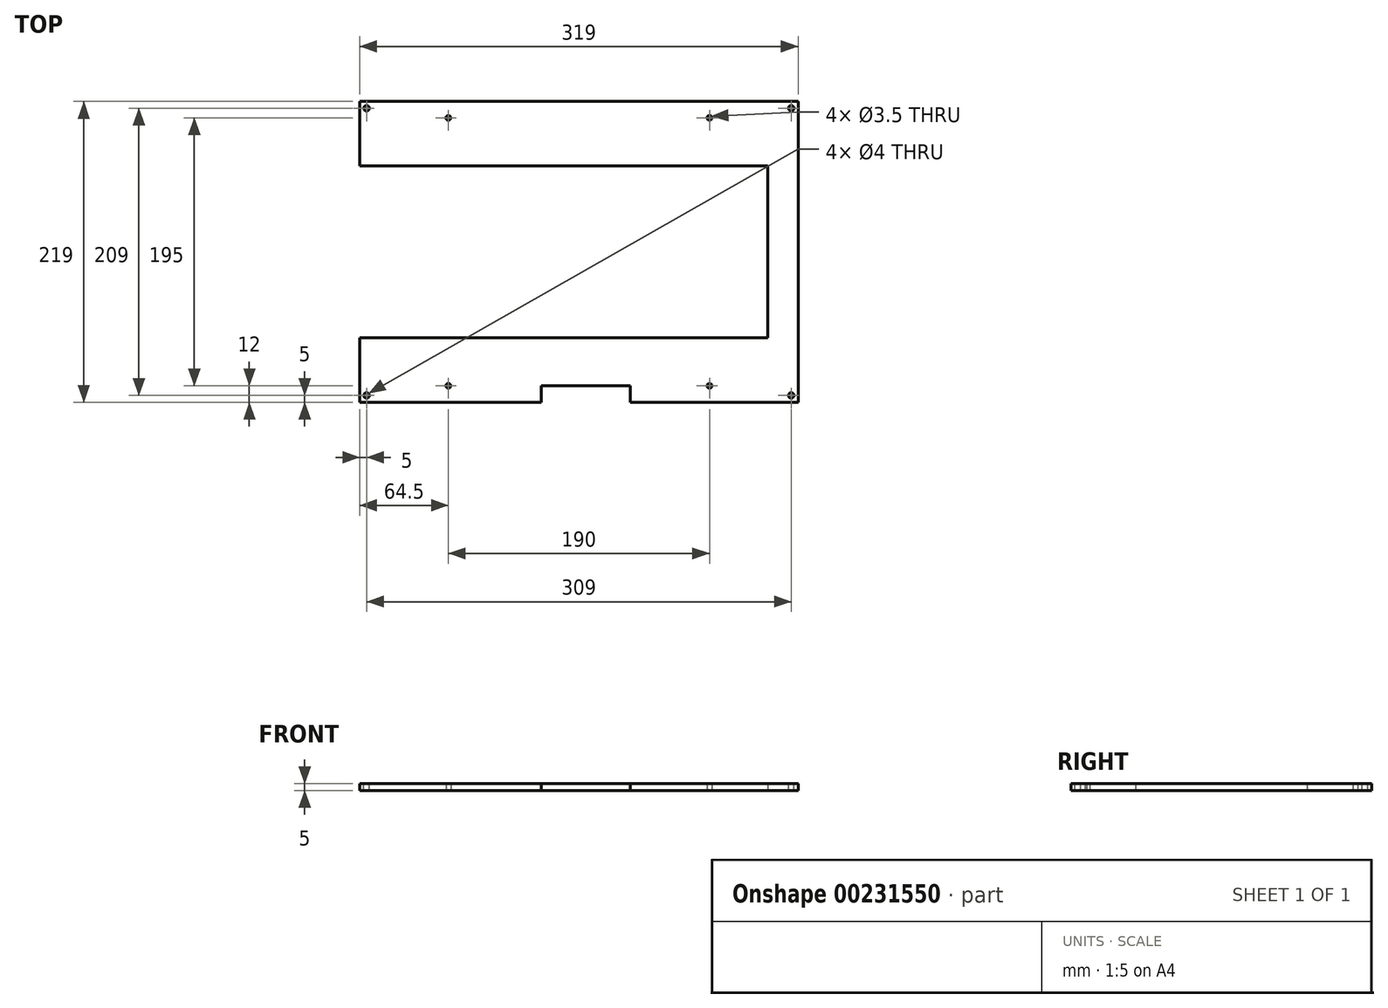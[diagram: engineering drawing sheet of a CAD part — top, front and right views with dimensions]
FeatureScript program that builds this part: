
annotation { "Feature Type Name" : "Feature", "Feature Type Description" : "" }
export const myFeature = defineFeature(function(context is Context, id is Id, definition is map)
    precondition{}
    {
        {
            var Q0;
            Q0=qCreatedBy(makeId("Top.planeOp"),FACE);
            var sketch = newSketch(context, id + "F0", { "sketchPlane" : qUnion([Q0])});
            skLineSegment(sketch, "E0.bottom", {"start": v(-157.5, 107.5) * mm, "end": v(157.5, 107.5) * mm});
            skLineSegment(sketch, "E0.top", {"start": v(-157.5, -107.5) * mm, "end": v(157.5, -107.5) * mm});
            skLineSegment(sketch, "E0.left", {"start": v(-157.5, 107.5) * mm, "end": v(-157.5, 62.5) * mm});
            skLineSegment(sketch, "E0.right", {"start": v(157.5, 107.5) * mm, "end": v(157.5, 62.5) * mm});
            skPoint(sketch, "E0.middle", {"position": v(0, 0) * mm});
            skLineSegment(sketch, "E1", {"start": v(-157.5, 62.5) * mm, "end": v(137.5, 62.5) * mm});
            skLineSegment(sketch, "E2", {"start": v(-157.5, 0) * mm, "end": v(157.5, 0) * mm, "construction": true});
            skLineSegment(sketch, "E3", {"start": v(0, 107.5) * mm, "end": v(0, -107.5) * mm, "construction": true});
            skLineSegment(sketch, "E4.trimOffspring", {"start": v(-157.5, -62.5) * mm, "end": v(-157.5, -107.5) * mm});
            skLineSegment(sketch, "E5.MirrorCS", {"start": v(-157.5, -62.5) * mm, "end": v(137.5, -62.5) * mm});
            skLineSegment(sketch, "E6.trimOffspring", {"start": v(157.5, -62.5) * mm, "end": v(157.5, -107.5) * mm});
            skCircle(sketch, "E7", {"center": v(-95, 97.5) * mm, "radius": 1.75 * mm});
            skCircle(sketch, "E8.MirrorC", {"center": v(95, 97.5) * mm, "radius": 1.75 * mm});
            skCircle(sketch, "E9.MirrorC", {"center": v(-95, -97.5) * mm, "radius": 1.75 * mm});
            skCircle(sketch, "E10.MirrorC", {"center": v(95, -97.5) * mm, "radius": 1.75 * mm});
            skLineSegment(sketch, "E11", {"start": v(157.5, 62.5) * mm, "end": v(157.5, -62.5) * mm});
            skLineSegment(sketch, "E12", {"start": v(137.5, 62.5) * mm, "end": v(137.5, -62.5) * mm});
            skSolve(sketch);
        }
        {
            var Q0;
            Q0=qSketchRegion(id+"F0",true);
            extrude(context, id + "F1", {"entities" : qUnion([Q0]), "depth" : 5 * mm});
        }
        {
            var Q0;
            Q0=makeQuery(id+"F1.opExtrude","CAP_FACE",FACE,{"disambiguationData":[OSD([sQuery(id+"F0.wireOp",EDGE,"E0.bottom"),sQuery(id+"F0.wireOp",EDGE,"E0.top"),sQuery(id+"F0.wireOp",EDGE,"E0.left"),sQuery(id+"F0.wireOp",EDGE,"E0.right")])],"isStart":false});
            var sketch = newSketch(context, id + "F2", { "sketchPlane" : qUnion([Q0])});
            skCircle(sketch, "E13", {"center": v(-154.5, -104.5) * mm, "radius": 2 * mm});
            skLineSegment(sketch, "E14", {"start": v(-157.5, 85) * mm, "end": v(157.5, 0) * mm, "construction": true});
            skCircle(sketch, "E15.MirrorC", {"center": v(154.5, 274.5) * mm, "radius": 2 * mm});
            skCircle(sketch, "E16.MirrorC", {"center": v(-59.58, 247.27) * mm, "radius": 2 * mm});
            skLineSegment(sketch, "E17", {"start": v(-27.5, -107.5) * mm, "end": v(-27.5, -97.5) * mm});
            skLineSegment(sketch, "E18", {"start": v(-27.5, -97.5) * mm, "end": v(37.5, -97.5) * mm});
            skLineSegment(sketch, "E19.0", {"start": v(-27.5, -107.5) * mm, "end": v(37.5, -107.5) * mm});
            skLineSegment(sketch, "E20", {"start": v(37.5, -97.5) * mm, "end": v(37.5, -107.5) * mm});
            skPoint(sketch, "E21.orphan", {"position": v(-157.5, -107.5) * mm});
            skLineSegment(sketch, "E22", {"start": v(0, 107.5) * mm, "end": v(0, -107.5) * mm, "construction": true});
            skPoint(sketch, "E22.endSnap0", {"position": v(5, -107.5) * mm});
            skLineSegment(sketch, "E23", {"start": v(-157.5, 0) * mm, "end": v(157.5, 0) * mm, "construction": true});
            skCircle(sketch, "E24.MirrorC", {"center": v(154.5, -104.5) * mm, "radius": 2 * mm});
            skCircle(sketch, "E25.MirrorC", {"center": v(-154.5, 104.5) * mm, "radius": 2 * mm});
            skCircle(sketch, "E26.MirrorC", {"center": v(154.5, 104.5) * mm, "radius": 2 * mm});
            skSolve(sketch);
        }
        {
            var Q0;
            Q0=qSketchRegion(id+"F2",true);
            extrude(context, id + "F3", {"entities" : qUnion([Q0]), "operationType" : NewBodyOperationType.REMOVE, "endBound" : BoundingType.THROUGH_ALL, "oppositeDirection" : true, "depth" : 25 * mm});
        }
        {
            var Q0;
            Q0=makeQuery(id+"F1.opExtrude","CAP_FACE",FACE,{"disambiguationData":[OSD([sQuery(id+"F0.wireOp",EDGE,"E0.bottom"),sQuery(id+"F0.wireOp",EDGE,"E0.top"),sQuery(id+"F0.wireOp",EDGE,"E0.left"),sQuery(id+"F0.wireOp",EDGE,"E0.right"),sQuery(id+"F0.wireOp",EDGE,"E1"),sQuery(id+"F0.wireOp",EDGE,"E4.trimOffspring"),sQuery(id+"F0.wireOp",EDGE,"E5.MirrorCS"),sQuery(id+"F0.wireOp",EDGE,"E6.trimOffspring"),sQuery(id+"F0.wireOp",EDGE,"E7"),sQuery(id+"F0.wireOp",EDGE,"E8.MirrorC"),sQuery(id+"F0.wireOp",EDGE,"E9.MirrorC"),sQuery(id+"F0.wireOp",EDGE,"E10.MirrorC"),sQuery(id+"F0.wireOp",EDGE,"E11"),sQuery(id+"F0.wireOp",EDGE,"E12")])],"isStart":false});
            var sketch = newSketch(context, id + "F4", { "sketchPlane" : qUnion([Q0])});
            skLineSegment(sketch, "E27.0", {"start": v(-157.5, 107.5) * mm, "end": v(-157.5, 62.5) * mm});
            skLineSegment(sketch, "E28.0", {"start": v(-157.5, 107.5) * mm, "end": v(157.5, 107.5) * mm});
            skLineSegment(sketch, "E29.0", {"start": v(157.5, 107.5) * mm, "end": v(157.5, -107.5) * mm});
            skLineSegment(sketch, "E30.0", {"start": v(37.5, -107.5) * mm, "end": v(157.5, -107.5) * mm});
            skLineSegment(sketch, "E31.0", {"start": v(-157.5, -107.5) * mm, "end": v(-27.5, -107.5) * mm});
            skLineSegment(sketch, "E32.0", {"start": v(-157.5, -62.5) * mm, "end": v(-157.5, -107.5) * mm});
            skLineSegment(sketch, "E33.0", {"start": v(-159.5, 109.5) * mm, "end": v(-159.5, 62.5) * mm});
            skLineSegment(sketch, "E33.1", {"start": v(-159.5, 109.5) * mm, "end": v(159.5, 109.5) * mm});
            skLineSegment(sketch, "E33.2", {"start": v(159.5, 109.5) * mm, "end": v(159.5, -109.5) * mm});
            skLineSegment(sketch, "E33.3", {"start": v(37.5, -109.5) * mm, "end": v(159.5, -109.5) * mm});
            skLineSegment(sketch, "E34", {"start": v(-157.5, 62.5) * mm, "end": v(-159.5, 62.5) * mm});
            skLineSegment(sketch, "E35", {"start": v(37.5, -109.5) * mm, "end": v(37.5, -107.5) * mm});
            skLineSegment(sketch, "E36.0", {"start": v(-159.5, -109.5) * mm, "end": v(-27.5, -109.5) * mm});
            skLineSegment(sketch, "E36.1", {"start": v(-159.5, -62.5) * mm, "end": v(-159.5, -109.5) * mm});
            skLineSegment(sketch, "E37", {"start": v(-27.5, -109.5) * mm, "end": v(-27.5, -107.5) * mm});
            skLineSegment(sketch, "E38", {"start": v(-157.5, -62.5) * mm, "end": v(-159.5, -62.5) * mm});
            skSolve(sketch);
        }
        {
            var Q0;
            Q0 = qSketchRegion(id + "F4", true);
            var Q1;
            Q1=makeQuery(id+"F1.opExtrude","CAP_VERTEX",VERTEX,{"disambiguationData":[OSD([sQuery(id+"F0.wireOp",EDGE,"E0.bottom"),sQuery(id+"F0.wireOp",EDGE,"E0.left")])],"isStart":true});
            extrude(context, id + "F5", {"entities" : qUnion([Q0]), "operationType" : NewBodyOperationType.ADD, "endBound" : BoundingType.UP_TO_VERTEX, "oppositeDirection" : true, "endBoundEntityVertex" : qUnion([Q1]), "depth" : 25 * mm});
        }
    });
